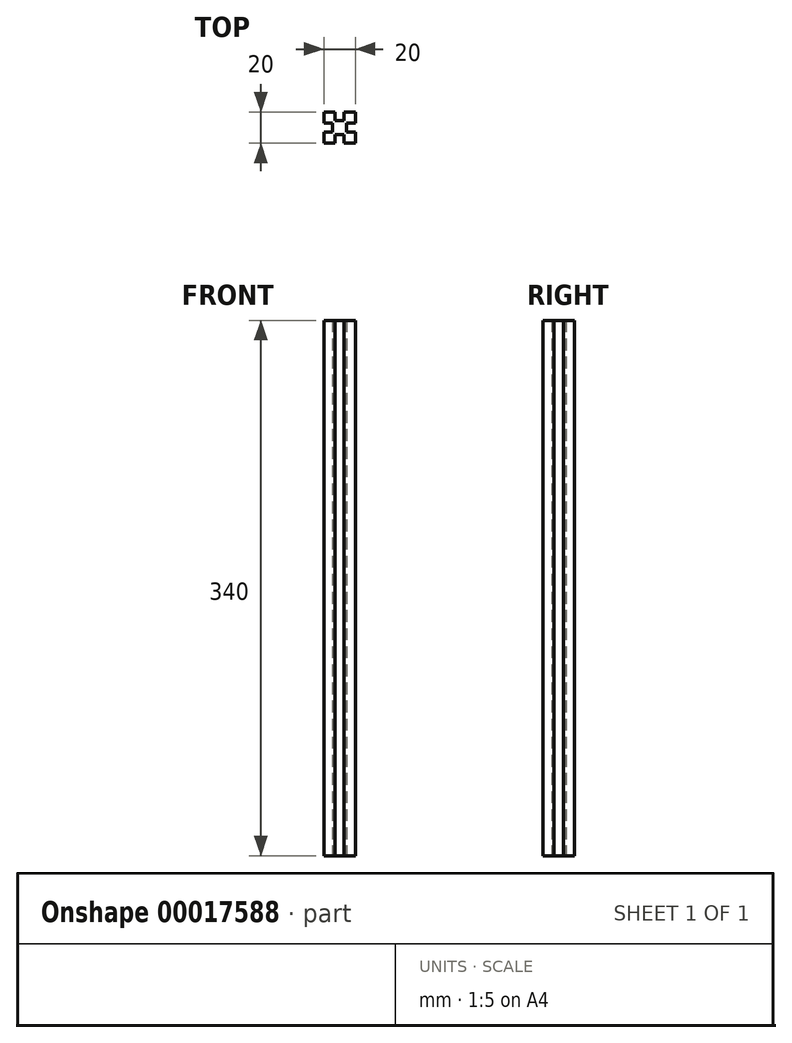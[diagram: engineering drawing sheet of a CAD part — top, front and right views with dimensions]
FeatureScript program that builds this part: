
annotation { "Feature Type Name" : "Feature", "Feature Type Description" : "" }
export const myFeature = defineFeature(function(context is Context, id is Id, definition is map)
    precondition{}
    {
        {
            var Q0;
            Q0=qCreatedBy(makeId("Top.planeOp"),FACE);
            var sketch = newSketch(context, id + "F0", { "sketchPlane" : qUnion([Q0])});
            skLineSegment(sketch, "E0.bottom", {"start": v(0, 0) * mm, "end": v(20, 0) * mm});
            skLineSegment(sketch, "E0.top", {"start": v(0, 20) * mm, "end": v(20, 20) * mm});
            skLineSegment(sketch, "E0.left", {"start": v(0, 0) * mm, "end": v(0, 20) * mm});
            skLineSegment(sketch, "E0.right", {"start": v(20, 0) * mm, "end": v(20, 20) * mm});
            skLineSegment(sketch, "E1.bottom", {"start": v(7, 20) * mm, "end": v(13, 20) * mm});
            skLineSegment(sketch, "E1.top", {"start": v(7, 14.5) * mm, "end": v(13, 14.5) * mm});
            skLineSegment(sketch, "E1.left", {"start": v(7, 20) * mm, "end": v(7, 14.5) * mm});
            skLineSegment(sketch, "E1.right", {"start": v(13, 20) * mm, "end": v(13, 14.5) * mm});
            skLineSegment(sketch, "E2.bottom", {"start": v(20, 13) * mm, "end": v(14.5, 13) * mm});
            skLineSegment(sketch, "E2.top", {"start": v(20, 7) * mm, "end": v(14.5, 7) * mm});
            skLineSegment(sketch, "E2.left", {"start": v(20, 13) * mm, "end": v(20, 7) * mm});
            skLineSegment(sketch, "E2.right", {"start": v(14.5, 13) * mm, "end": v(14.5, 7) * mm});
            skLineSegment(sketch, "E3.bottom", {"start": v(13, 0) * mm, "end": v(7, 0) * mm});
            skLineSegment(sketch, "E3.top", {"start": v(13, 5.5) * mm, "end": v(7, 5.5) * mm});
            skLineSegment(sketch, "E3.left", {"start": v(13, 0) * mm, "end": v(13, 5.5) * mm});
            skLineSegment(sketch, "E3.right", {"start": v(7, 0) * mm, "end": v(7, 5.5) * mm});
            skLineSegment(sketch, "E4.bottom", {"start": v(0, 7) * mm, "end": v(5.5, 7) * mm});
            skLineSegment(sketch, "E4.top", {"start": v(0, 13) * mm, "end": v(5.5, 13) * mm});
            skLineSegment(sketch, "E4.left", {"start": v(0, 7) * mm, "end": v(0, 13) * mm});
            skLineSegment(sketch, "E4.right", {"start": v(5.5, 7) * mm, "end": v(5.5, 13) * mm});
            skSolve(sketch);
        }
        {
            var Q0;
            Q0=makeQuery(id+"F0.imprint","IMPRINT",FACE,{"disambiguationData":[TD([[makeQuery(id+"F0.imprint","IMPRINT",EDGE,{"derivedFrom":sQuery(id+"F0.wireOp",EDGE,"E1.top")}),-1.0]])]});
            extrude(context, id + "F1", {"entities" : qUnion([Q0]), "depth" : 340 * mm});
        }
    });
